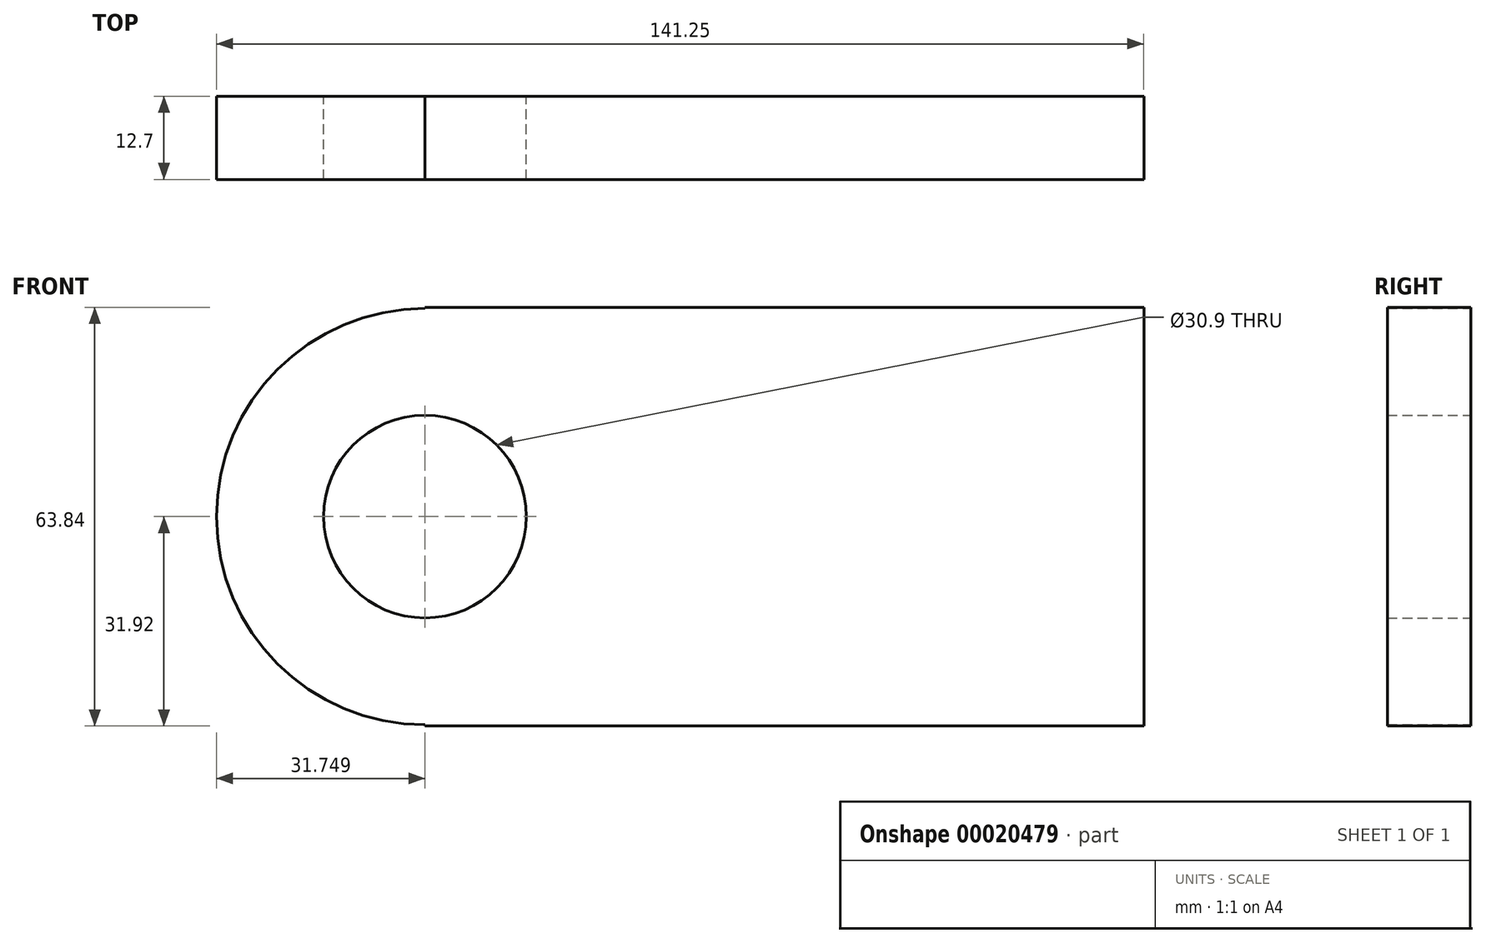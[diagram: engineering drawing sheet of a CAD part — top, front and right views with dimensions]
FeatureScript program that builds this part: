
annotation { "Feature Type Name" : "Feature", "Feature Type Description" : "" }
export const myFeature = defineFeature(function(context is Context, id is Id, definition is map)
    precondition{}
    {
        {
            var Q0;
            Q0=qCreatedBy(makeId("Front.planeOp"),FACE);
            var sketch = newSketch(context, id + "F0", { "sketchPlane" : qUnion([Q0])});
            skLineSegment(sketch, "E0.rect.bottom", {"start": v(-53.16, 31.92) * mm, "end": v(56.34, 31.92) * mm});
            skLineSegment(sketch, "E0.rect.top", {"start": v(-53.16, -31.92) * mm, "end": v(56.34, -31.92) * mm});
            skLineSegment(sketch, "E0.rect.left", {"start": v(-53.16, 31.92) * mm, "end": v(-53.16, -31.92) * mm});
            skLineSegment(sketch, "E0.rect.right", {"start": v(56.34, 31.92) * mm, "end": v(56.34, -31.92) * mm});
            skPoint(sketch, "E0.rect.middle", {"position": v(1.6, 0) * mm});
            skCircle(sketch, "E1", {"center": v(-53.16, 0) * mm, "radius": 31.75 * mm});
            skCircle(sketch, "E2", {"center": v(-53.16, 0) * mm, "radius": 15.45 * mm});
            skSolve(sketch);
        }
        {
            var Q0;
            Q0 = qSketchRegion(id + "F0", true);
            extrude(context, id + "F1", {"entities" : qUnion([Q0]), "depth" : 12.7 * mm});
        }
    });
